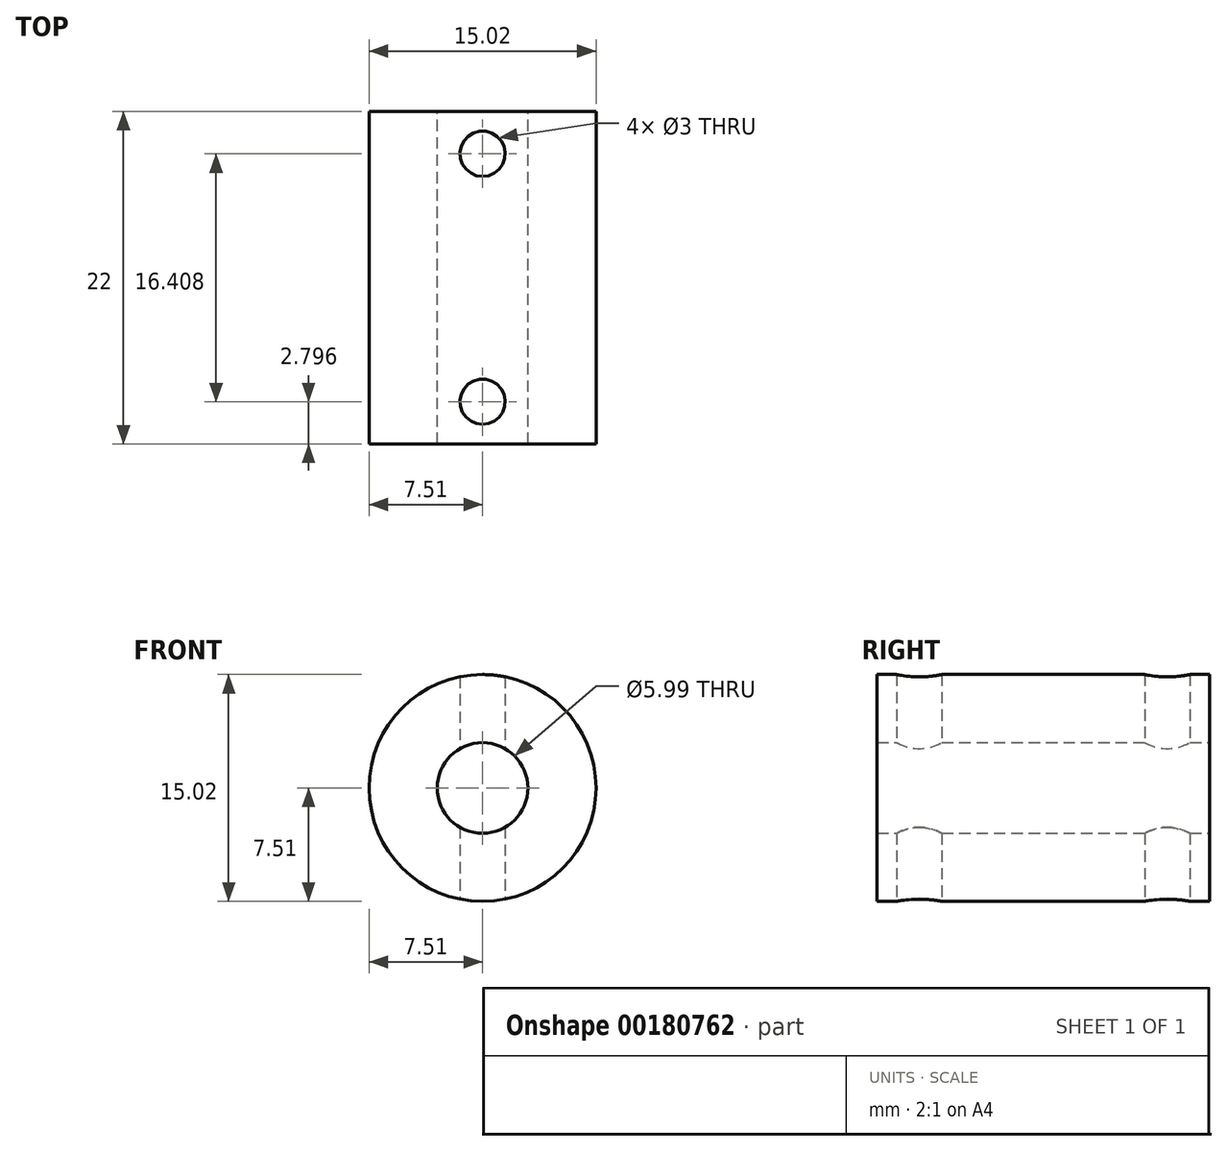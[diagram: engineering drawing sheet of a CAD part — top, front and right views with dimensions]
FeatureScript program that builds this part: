
annotation { "Feature Type Name" : "Feature", "Feature Type Description" : "" }
export const myFeature = defineFeature(function(context is Context, id is Id, definition is map)
    precondition{}
    {
        {
            var Q0;
            Q0=qCreatedBy(makeId("Front.planeOp"),FACE);
            var sketch = newSketch(context, id + "F0", { "sketchPlane" : qUnion([Q0])});
            skCircle(sketch, "E0", {"center": v(0, 0) * mm, "radius": 7.5 * mm});
            skCircle(sketch, "E1", {"center": v(0, 0) * mm, "radius": 3 * mm});
            skSolve(sketch);
        }
        {
            var Q0;
            Q0 = qSketchRegion(id + "F0", true);
            extrude(context, id + "F1", {"entities" : qUnion([Q0]), "endBound" : BoundingType.SYMMETRIC, "depth" : 22 * mm});
        }
        {
            var Q0;
            Q0=qCreatedBy(makeId("Top.planeOp"),FACE);
            var sketch = newSketch(context, id + "F2", { "sketchPlane" : qUnion([Q0])});
            skCircle(sketch, "E2", {"center": v(0, 8.2) * mm, "radius": 1.5 * mm});
            skCircle(sketch, "E3", {"center": v(0, -8.2) * mm, "radius": 1.5 * mm});
            skSolve(sketch);
        }
        {
            var Q0;
            Q0 = qSketchRegion(id + "F2", true);
            extrude(context, id + "F3", {"entities" : qUnion([Q0]), "operationType" : NewBodyOperationType.REMOVE, "endBound" : BoundingType.THROUGH_ALL, "depth" : 25.4 * mm, "hasSecondDirection" : true, "secondDirectionBound" : SecondDirectionBoundingType.THROUGH_ALL, "secondDirectionOppositeDirection" : true, "secondDirectionDepth" : 25.4 * mm});
        }
    });
